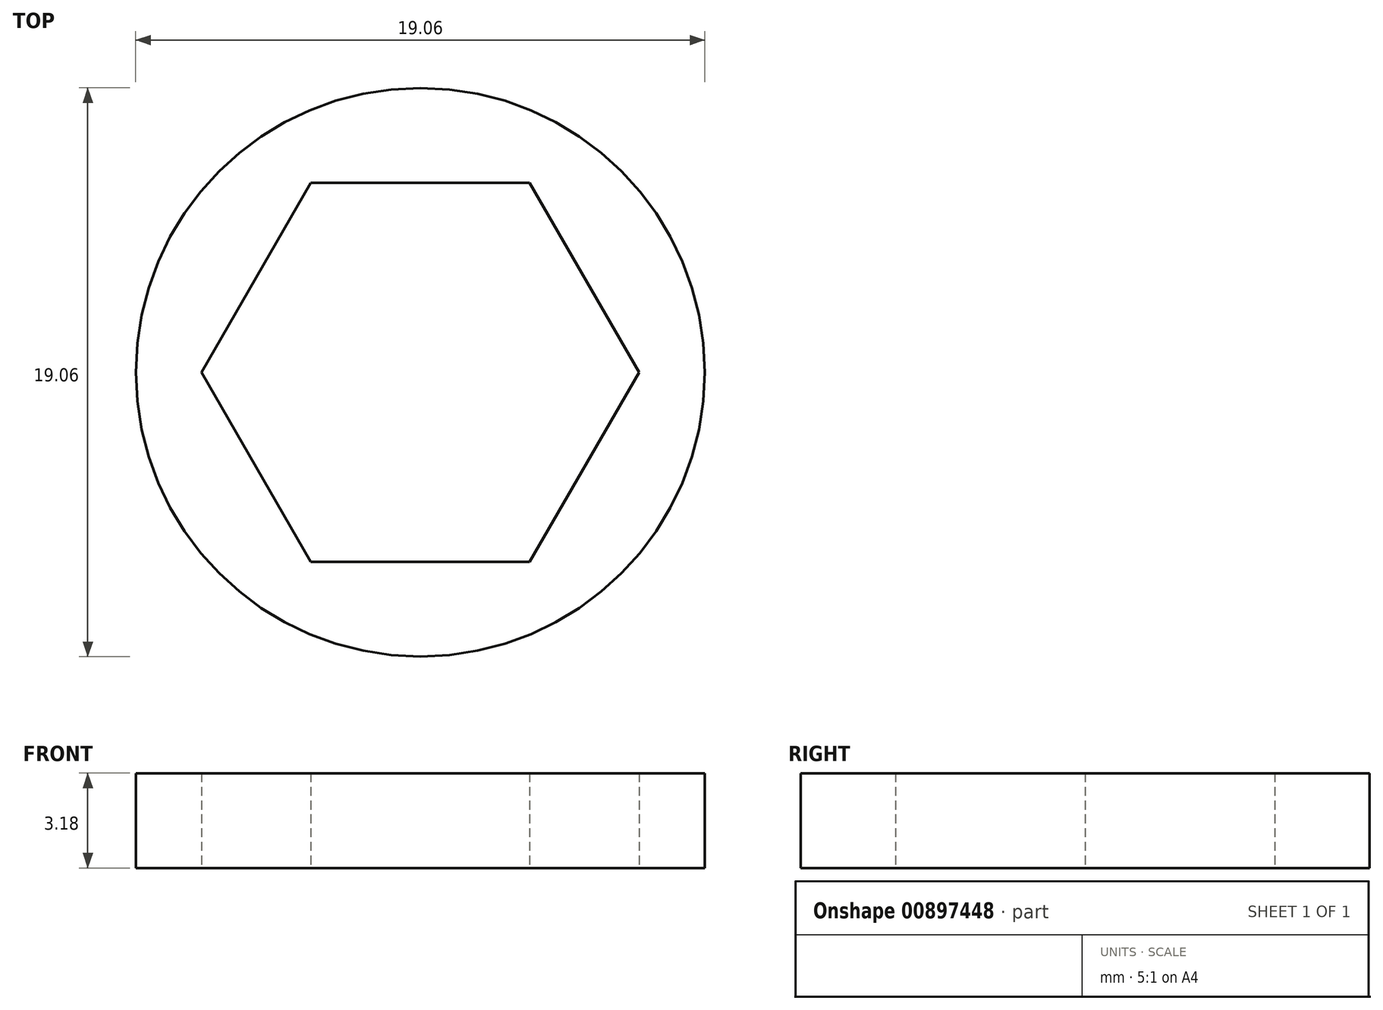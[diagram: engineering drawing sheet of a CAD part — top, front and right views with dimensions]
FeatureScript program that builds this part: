
annotation { "Feature Type Name" : "Feature", "Feature Type Description" : "" }
export const myFeature = defineFeature(function(context is Context, id is Id, definition is map)
    precondition{}
    {
        {
            var Q0;
            Q0=qCreatedBy(makeId("Top.planeOp"),FACE);
            var sketch = newSketch(context, id + "F0", { "sketchPlane" : qUnion([Q0])});
            skCircle(sketch, "E0", {"center": v(0, 0) * mm, "radius": 9.53 * mm});
            skCircle(sketch, "E1.cCircle", {"center": v(0, 0) * mm, "radius": 6.35 * mm, "construction": true});
            skLineSegment(sketch, "E1.0", {"start": v(-3.67, 6.35) * mm, "end": v(3.67, 6.35) * mm});
            skLineSegment(sketch, "E1.1", {"start": v(3.67, 6.35) * mm, "end": v(7.33, 0) * mm});
            skLineSegment(sketch, "E1.2", {"start": v(7.33, 0) * mm, "end": v(3.67, -6.35) * mm});
            skLineSegment(sketch, "E1.3", {"start": v(3.67, -6.35) * mm, "end": v(-3.67, -6.35) * mm});
            skLineSegment(sketch, "E1.4", {"start": v(-3.67, -6.35) * mm, "end": v(-7.33, 0) * mm});
            skLineSegment(sketch, "E1.5", {"start": v(-7.33, 0) * mm, "end": v(-3.67, 6.35) * mm});
            skPoint(sketch, "E1.0.midPoint", {"position": v(0, 6.35) * mm});
            skSolve(sketch);
        }
        {
            var Q0;
            Q0 = qSketchRegion(id + "F0", true);
            extrude(context, id + "F1", {"entities" : qUnion([Q0]), "depth" : 3.17 * mm, "offsetDistance" : 25.4 * mm});
        }
    });
